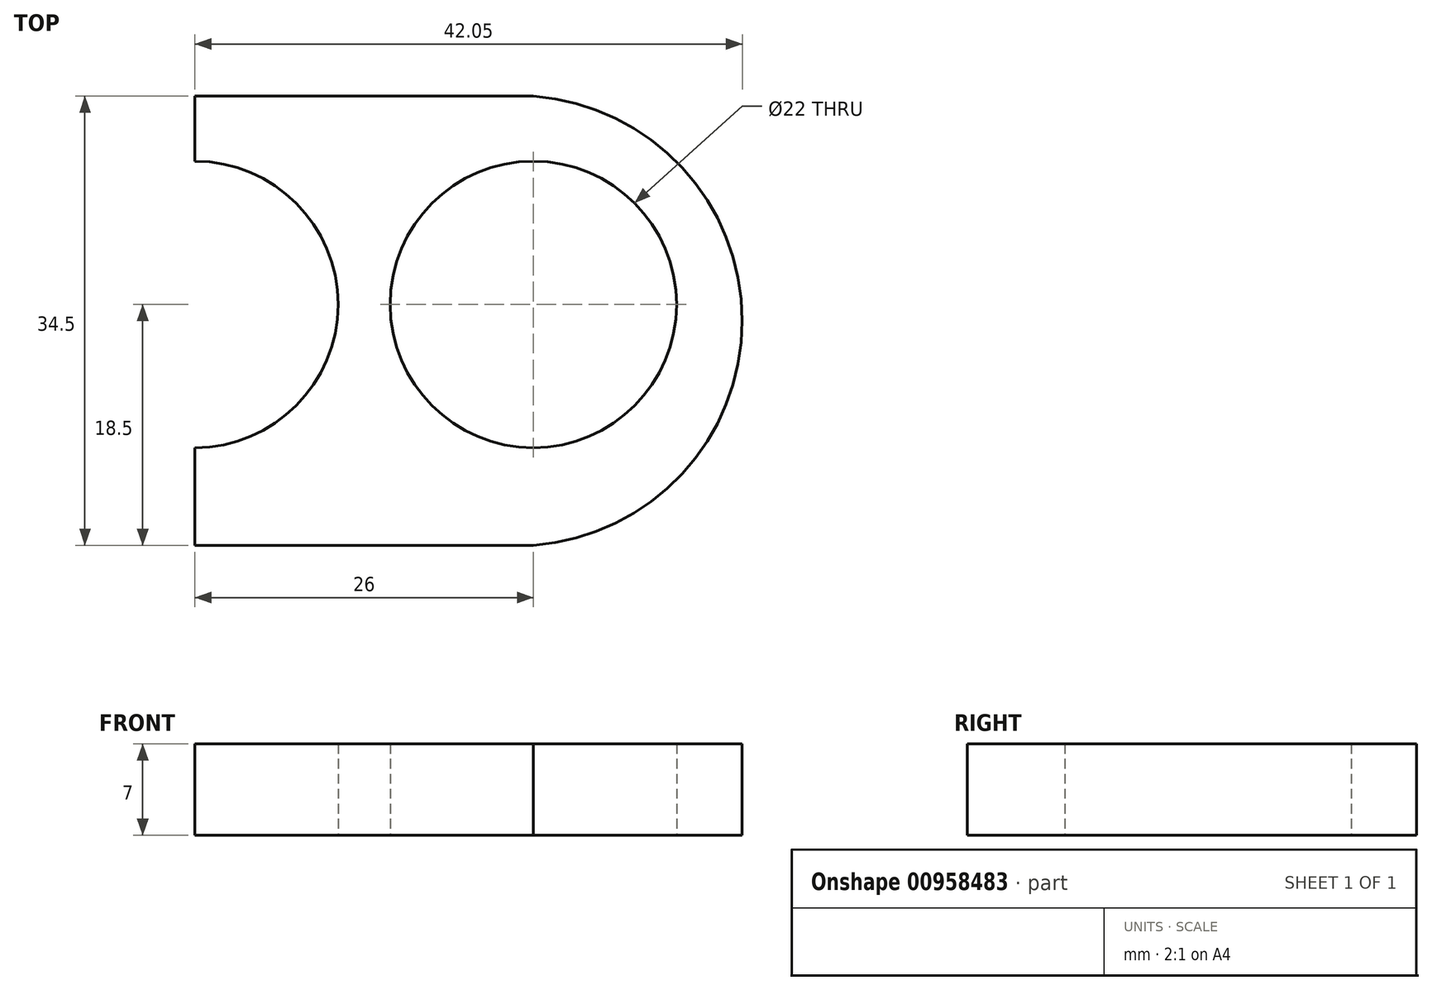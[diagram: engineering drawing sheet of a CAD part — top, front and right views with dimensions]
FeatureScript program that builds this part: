
annotation { "Feature Type Name" : "Feature", "Feature Type Description" : "" }
export const myFeature = defineFeature(function(context is Context, id is Id, definition is map)
    precondition{}
    {
        {
            var Q0;
            Q0=qCreatedBy(makeId("Top.planeOp"),FACE);
            var sketch = newSketch(context, id + "F0", { "sketchPlane" : qUnion([Q0])});
            skCircle(sketch, "E0", {"center": v(0, 0) * mm, "radius": 11 * mm});
            skLineSegment(sketch, "E1", {"start": v(0, 0) * mm, "end": v(26, 0) * mm, "construction": true});
            skCircle(sketch, "E2", {"center": v(26, 0) * mm, "radius": 11 * mm});
            skLineSegment(sketch, "E3", {"start": v(26, 0) * mm, "end": v(26, 16) * mm, "construction": true});
            skLineSegment(sketch, "E4", {"start": v(26, 0) * mm, "end": v(26, -18.5) * mm, "construction": true});
            skLineSegment(sketch, "E5", {"start": v(26, 0) * mm, "end": v(42, 0) * mm, "construction": true});
            skArc(sketch, "E6", {"start": v(26, -18.5) * mm, "mid": v(42.05, -1.25) * mm, "end": v(26, 16) * mm});
            skLineSegment(sketch, "E7", {"start": v(26, 16) * mm, "end": v(0, 16) * mm});
            skLineSegment(sketch, "E8", {"start": v(26, -18.5) * mm, "end": v(0, -18.5) * mm});
            skLineSegment(sketch, "E9", {"start": v(0, 16) * mm, "end": v(0, 11) * mm});
            skLineSegment(sketch, "E10", {"start": v(0, -18.5) * mm, "end": v(0, -11) * mm});
            skSolve(sketch);
        }
        {
            var Q0;
            Q0=makeQuery(id+"F0.imprint","IMPRINT",FACE,{"disambiguationData":[TD([[makeQuery(id+"F0.imprint","IMPRINT",EDGE,{"derivedFrom":sQuery(id+"F0.wireOp",EDGE,"E2")}),-1.0]])]});
            extrude(context, id + "F1", {"entities" : qUnion([Q0]), "depth" : 7 * mm, "offsetDistance" : 25 * mm});
        }
    });
